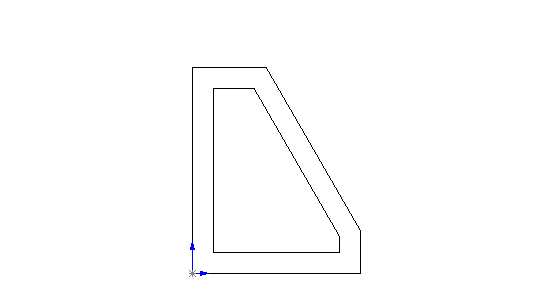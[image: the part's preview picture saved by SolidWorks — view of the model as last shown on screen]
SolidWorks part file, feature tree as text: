
SOLIDWORKS PART (.sldprt)
format: sldprt  version: not decoded by parser v0  size: 126,464 bytes
history: native  units: mm
features: sketch x2, extrude x1, shell x1, cut_extrude x1 (+11 scaffold rows collapsed)
feature tree (16):
  scaffold x11  (default folders/planes/origin — collapsed)
  sketch  "Sketch1"  dims[c1.D1=406.4mm c1.D2=101.6mm c1.D3=177.8mm c1.D4=101.6mm c2.D4=30.0deg c2.D5=~497.546815mm]
  extrude  "Extrude1"  Depth=609.6mm
  shell  "Shell2"  Thickness=50.8mm
  sketch  "Sketch4"  dims[D1=50.8mm]
  cut_extrude  "Cut-Extrude1"  Depth=55.88mm Thickness=50.8mm
decode coverage: 5 of 5 modeling features carry decoded parameters
note: ~ marks probable driven/reference dimensions
note: suppression state not decoded; provenance and decode notes live in map.json
